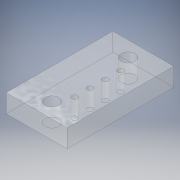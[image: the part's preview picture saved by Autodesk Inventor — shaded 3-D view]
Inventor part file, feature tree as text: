
AUTODESK INVENTOR PART (.ipt)
format: ipt  version: 2019 (Build 230136000, 136)  size: 135,168 bytes
history: native  units: mm
features: extrude x1, sketch x1
ambient origin geometry x8: Origin, YZ Plane, XZ Plane, XY Plane, X Axis, Y Axis, Z Axis, Center Point
bodies: Body1 (feature_tree)
feature tree (2):
  extrude  "Extrusion2"  Depth=20.0mm
  sketch  "Sketch2"  dims[d31=6.0mm d32=0.0mm d76=20.0mm d77=35.0mm d78=5.0mm d79=25.0mm d80=10.0mm d81=4.5mm d82=1.9mm d83=40.0mm d85=5.0mm d86=10.0mm d88=10.0mm d90=5.0mm d91=7.5mm]
